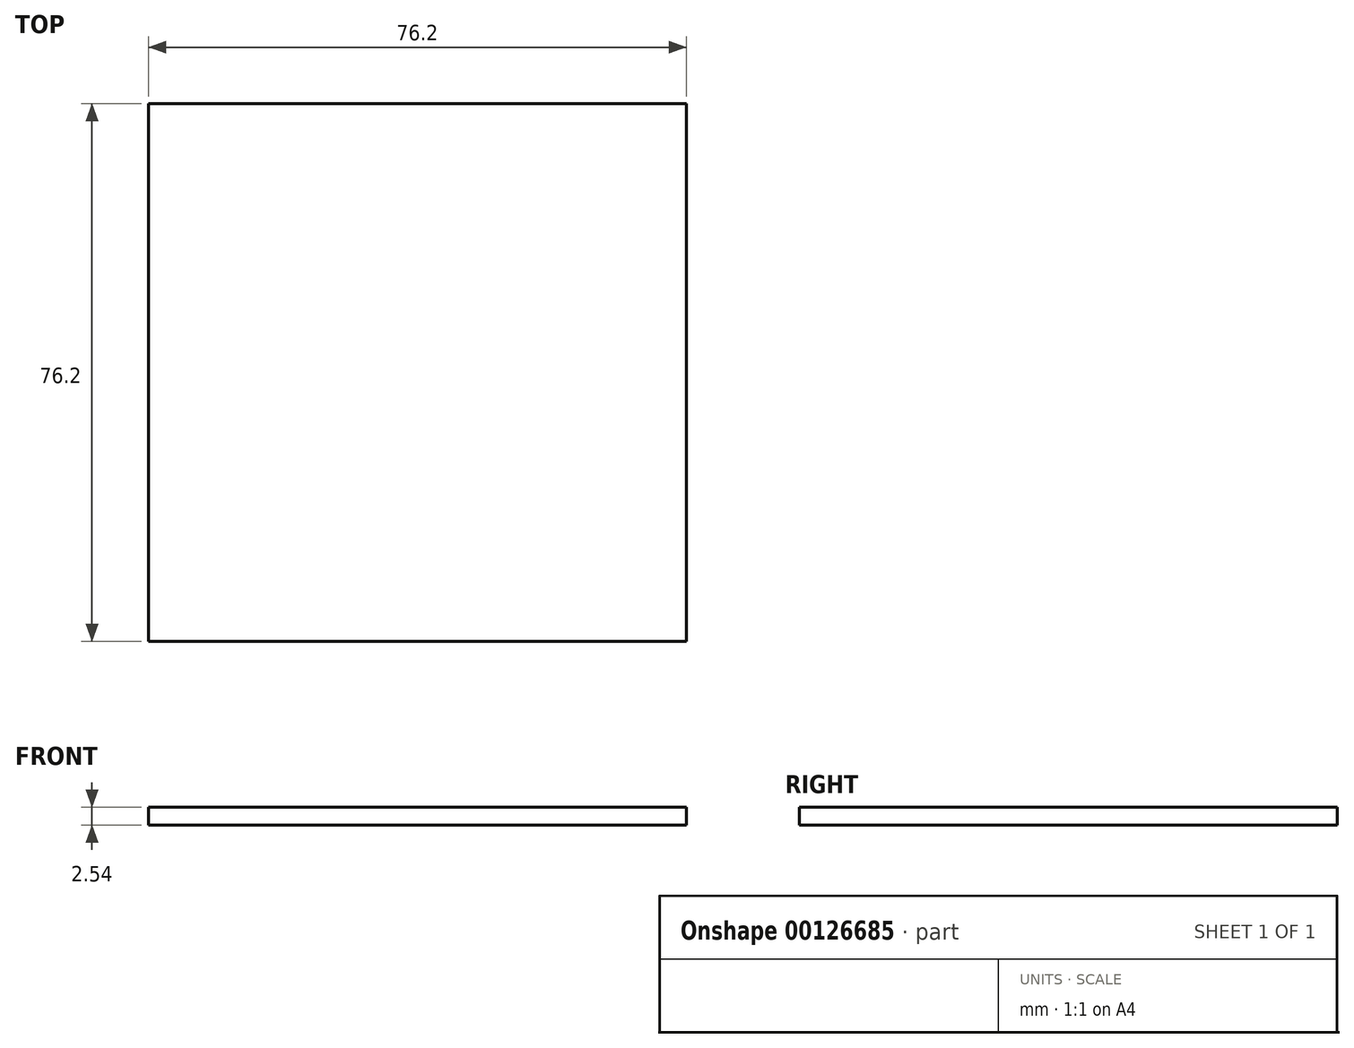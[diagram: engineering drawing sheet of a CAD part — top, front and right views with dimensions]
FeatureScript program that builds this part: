
annotation { "Feature Type Name" : "Feature", "Feature Type Description" : "" }
export const myFeature = defineFeature(function(context is Context, id is Id, definition is map)
    precondition{}
    {
        {
            var Q0;
            Q0=qCreatedBy(makeId("Top.planeOp"),FACE);
            var sketch = newSketch(context, id + "F0", { "sketchPlane" : qUnion([Q0])});
            skLineSegment(sketch, "E0.bottom", {"start": v(0, 0) * mm, "end": v(-76.2, 0) * mm});
            skLineSegment(sketch, "E0.top", {"start": v(0, 76.2) * mm, "end": v(-76.2, 76.2) * mm});
            skLineSegment(sketch, "E0.left", {"start": v(0, 0) * mm, "end": v(0, 76.2) * mm});
            skLineSegment(sketch, "E0.right", {"start": v(-76.2, 0) * mm, "end": v(-76.2, 76.2) * mm});
            skSolve(sketch);
        }
        {
            var Q0;
            Q0=makeQuery(id+"F0.imprint","IMPRINT",FACE,{"disambiguationData":[TD([[makeQuery(id+"F0.imprint","IMPRINT",EDGE,{"derivedFrom":sQuery(id+"F0.wireOp",EDGE,"E0.bottom")}),-1.0]])]});
            extrude(context, id + "F1", {"entities" : qUnion([Q0]), "depth" : 2.54 * mm});
        }
    });
